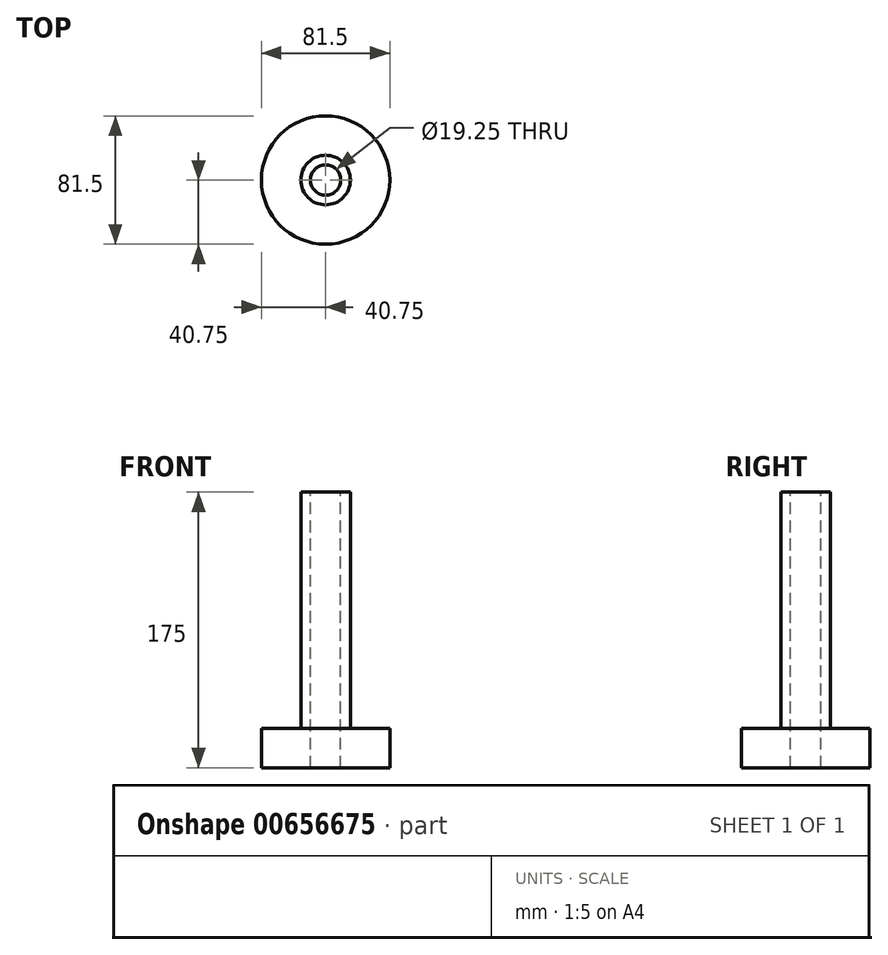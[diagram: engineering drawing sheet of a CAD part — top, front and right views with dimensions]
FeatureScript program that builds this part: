
annotation { "Feature Type Name" : "Feature", "Feature Type Description" : "" }
export const myFeature = defineFeature(function(context is Context, id is Id, definition is map)
    precondition{}
    {
        {
            var Q0;
            Q0=qCreatedBy(makeId("Front.planeOp"),FACE);
            var sketch = newSketch(context, id + "F0", { "sketchPlane" : qUnion([Q0])});
            skLineSegment(sketch, "E0", {"start": v(0, 0) * mm, "end": v(0, 150) * mm, "construction": true});
            skLineSegment(sketch, "E1.bottom", {"start": v(15.75, 0) * mm, "end": v(9.63, 0) * mm});
            skLineSegment(sketch, "E1.top", {"start": v(15.75, 150) * mm, "end": v(9.62, 150) * mm});
            skLineSegment(sketch, "E1.left", {"start": v(15.75, 0) * mm, "end": v(15.75, 150) * mm});
            skLineSegment(sketch, "E1.right", {"start": v(9.63, 0) * mm, "end": v(9.62, 150) * mm});
            skLineSegment(sketch, "E2.bottom", {"start": v(9.62, 150) * mm, "end": v(40.75, 150) * mm});
            skLineSegment(sketch, "E2.top", {"start": v(9.62, 175) * mm, "end": v(40.75, 175) * mm});
            skLineSegment(sketch, "E2.left", {"start": v(9.62, 150) * mm, "end": v(9.62, 175) * mm});
            skLineSegment(sketch, "E2.right", {"start": v(40.75, 150) * mm, "end": v(40.75, 175) * mm});
            skSolve(sketch);
        }
        {
            var Q0;
            {var subQ0=makeQuery(id+"F0.imprint","IMPRINT",EDGE,{"derivedFrom":sQuery(id+"F0.wireOp",EDGE,"E1.top")});Q0=qUnion([makeQuery(id+"F0.imprint","IMPRINT",FACE,{"disambiguationData":[TD([[makeQuery(id+"F0.imprint","IMPRINT",EDGE,{"derivedFrom":sQuery(id+"F0.wireOp",EDGE,"E1.bottom")}),-1.0]])]}),makeQuery(id+"F0.imprint","IMPRINT",FACE,{"disambiguationData":[TD([[subQ0,-1.0]])]})]);}
            var Q1;
            Q1=sQuery(id+"F0.wireOp",EDGE,"E0");
            revolve(context, id + "F1", {"entities" : qUnion([Q0]), "axis" : qUnion([Q1]), "revolveType" : RevolveType.FULL});
        }
        {
            var Q0;
            Q0=qCreatedBy(makeId("Top.planeOp"),FACE);
            var sketch = newSketch(context, id + "F2", { "sketchPlane" : qUnion([Q0])});
            skLineSegment(sketch, "E3", {"start": v(0, 0) * mm, "end": v(7.31, 37.52) * mm});
            skSolve(sketch);
        }
        {
            var Q0;
            Q0=makeQuery(id+"F1.opRevolve","SWEPT_BODY",BODY,{"disambiguationData":[OSD([sQuery(id+"F0.wireOp",EDGE,"E1.bottom"),sQuery(id+"F0.wireOp",EDGE,"E1.left"),sQuery(id+"F0.wireOp",EDGE,"E1.right"),sQuery(id+"F0.wireOp",EDGE,"E2.bottom"),sQuery(id+"F0.wireOp",EDGE,"E2.top"),sQuery(id+"F0.wireOp",EDGE,"E2.left"),sQuery(id+"F0.wireOp",EDGE,"E2.right")])]});
            var Q1;
            Q1=sQuery(id+"F2.wireOp",EDGE,"E3");
            transform(context, id + "F3", {"entities" : qUnion([Q0]), "transformType" : TransformType.ROTATION, "transformAxis" : qUnion([Q1]), "angle" : 180 * degree, "makeCopy" : false});
        }
    });
